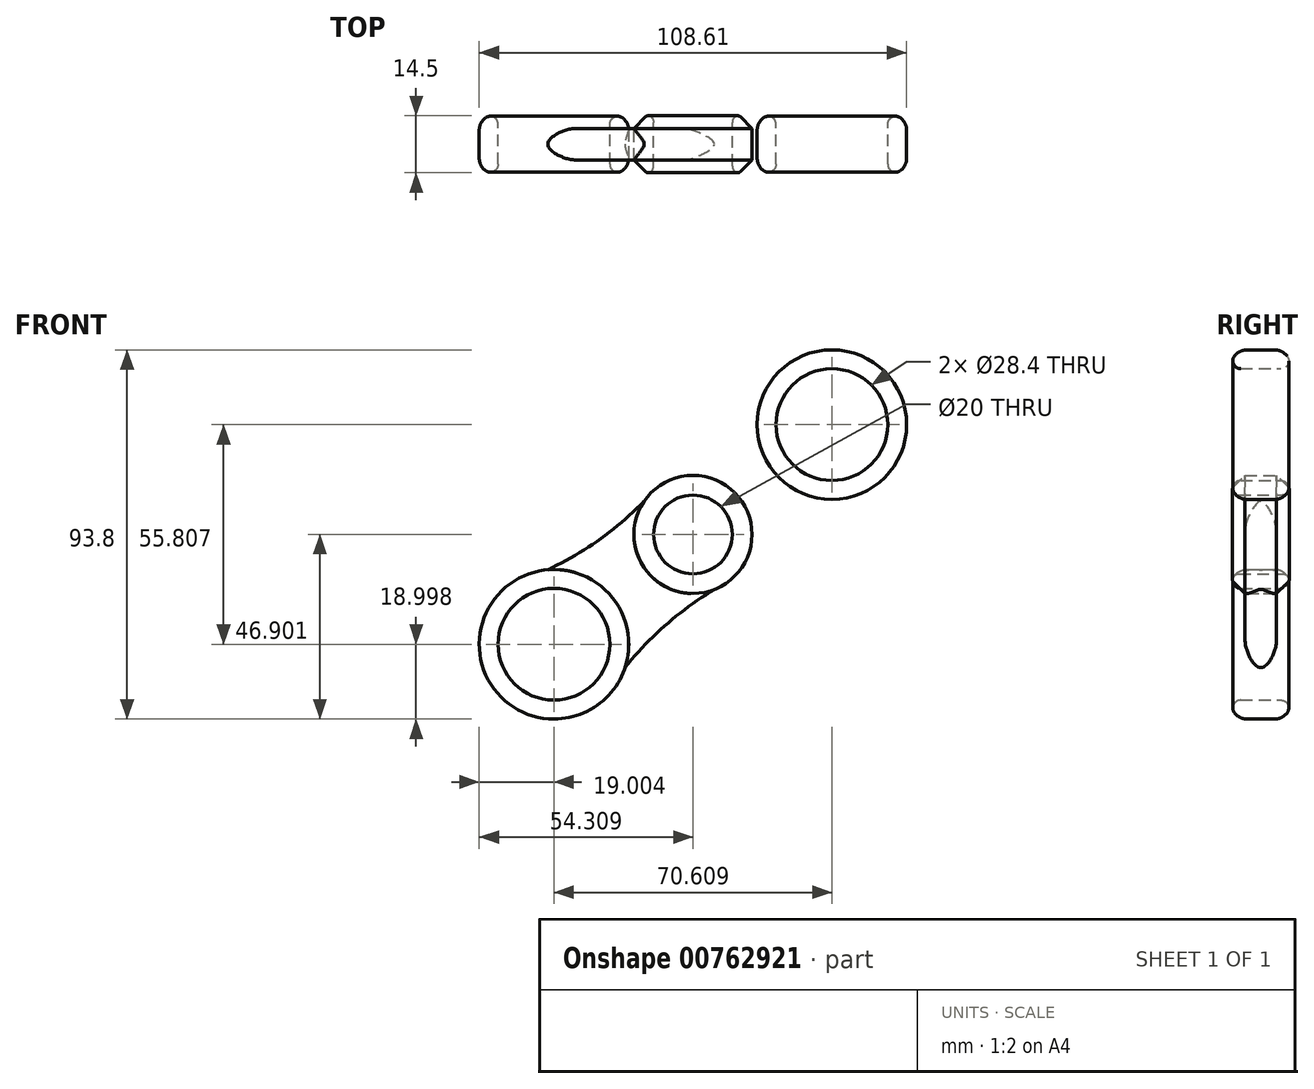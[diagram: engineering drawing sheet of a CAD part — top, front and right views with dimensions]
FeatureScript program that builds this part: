
annotation { "Feature Type Name" : "Feature", "Feature Type Description" : "" }
export const myFeature = defineFeature(function(context is Context, id is Id, definition is map)
    precondition{}
    {
        {
            var Q0;
            Q0=qCreatedBy(makeId("Front.planeOp"),FACE);
            var sketch = newSketch(context, id + "F0", { "sketchPlane" : qUnion([Q0])});
            skCircle(sketch, "E0", {"center": v(-102.67, -16) * mm, "radius": 14.2 * mm});
            skCircle(sketch, "E1", {"center": v(-32.06, 39.8) * mm, "radius": 14.2 * mm});
            skLineSegment(sketch, "E2", {"start": v(-32.06, 39.8) * mm, "end": v(-102.67, -16) * mm});
            skCircle(sketch, "E3", {"center": v(-67.36, 11.9) * mm, "radius": 15 * mm});
            skCircle(sketch, "E4", {"center": v(-102.67, -16) * mm, "radius": 19 * mm});
            skCircle(sketch, "E5", {"center": v(-32.06, 39.8) * mm, "radius": 19 * mm});
            skLineSegment(sketch, "E6", {"start": v(-79.13, 2.6) * mm, "end": v(-87.76, -4.22) * mm});
            skLineSegment(sketch, "E7", {"start": v(-87.76, -4.22) * mm, "end": v(-55.6, 21.2) * mm});
            skLineSegment(sketch, "E8", {"start": v(-55.6, 21.2) * mm, "end": v(-46.96, 28.02) * mm});
            skArc(sketch, "E9", {"start": v(-58.23, 0) * mm, "mid": v(-76.64, -13.26) * mm, "end": v(-90.88, -30.9) * mm});
            skCircle(sketch, "E10", {"center": v(-67.36, 11.9) * mm, "radius": 10 * mm});
            skArc(sketch, "E11", {"start": v(-76.66, 23.67) * mm, "mid": v(-58.15, 36.97) * mm, "end": v(-43.84, 54.71) * mm});
            skArc(sketch, "E12", {"start": v(-20.28, 24.9) * mm, "mid": v(-40.95, 15.03) * mm, "end": v(-58.23, 0) * mm});
            skArc(sketch, "E13", {"start": v(-114.45, -1.1) * mm, "mid": v(-93.88, 8.73) * mm, "end": v(-76.66, 23.67) * mm});
            skSolve(sketch);
        }
        {
            var Q0;
            {var subQ0=sQuery(id+"F0.wireOp",EDGE,"E11");var subQ1=sQuery(id+"F0.wireOp",EDGE,"E3");var subQ3=makeQuery(id+"F0.imprint","INTERSECT",VERTEX,{"derivedFrom":[subQ1,subQ0]});Q0=makeQuery(id+"F0.imprint","IMPRINT",FACE,{"disambiguationData":[TD([[makeQuery(id+"F0.imprint","IMPRINT",EDGE,{"disambiguationData":[TD([[subQ3,-1.0]])],"derivedFrom":subQ1}),1.0]])]});}
            var Q1;
            {var subQ0=sQuery(id+"F0.wireOp",EDGE,"E13");var subQ1=sQuery(id+"F0.wireOp",EDGE,"E3");var subQ3=makeQuery(id+"F0.imprint","INTERSECT",VERTEX,{"derivedFrom":[subQ1,subQ0]});Q1=makeQuery(id+"F0.imprint","IMPRINT",FACE,{"disambiguationData":[TD([[makeQuery(id+"F0.imprint","IMPRINT",EDGE,{"disambiguationData":[TD([[subQ3,1.0]])],"derivedFrom":subQ1}),1.0]])]});}
            var Q2;
            {var subQ0=sQuery(id+"F0.wireOp",EDGE,"E9");var subQ1=sQuery(id+"F0.wireOp",EDGE,"E3");var subQ3=makeQuery(id+"F0.imprint","INTERSECT",VERTEX,{"derivedFrom":[subQ1,subQ0]});Q2=makeQuery(id+"F0.imprint","IMPRINT",FACE,{"disambiguationData":[TD([[makeQuery(id+"F0.imprint","IMPRINT",EDGE,{"disambiguationData":[TD([[subQ3,-1.0]])],"derivedFrom":subQ1}),1.0]])]});}
            var Q3;
            {var subQ0=sQuery(id+"F0.wireOp",EDGE,"E12");var subQ1=sQuery(id+"F0.wireOp",EDGE,"E3");var subQ3=makeQuery(id+"F0.imprint","INTERSECT",VERTEX,{"derivedFrom":[subQ1,subQ0]});Q3=makeQuery(id+"F0.imprint","IMPRINT",FACE,{"disambiguationData":[TD([[makeQuery(id+"F0.imprint","IMPRINT",EDGE,{"disambiguationData":[TD([[subQ3,1.0]])],"derivedFrom":subQ1}),1.0]])]});}
            var Q4;
            {var subQ0=sQuery(id+"F0.wireOp",EDGE,"E13");var subQ1=sQuery(id+"F0.wireOp",EDGE,"E4");var subQ2=makeQuery(id+"F0.imprint","INTERSECT",VERTEX,{"disambiguationData":[OD(0.0)],"derivedFrom":[subQ1,subQ0]});Q4=makeQuery(id+"F0.imprint","IMPRINT",FACE,{"disambiguationData":[TD([[makeQuery(id+"F0.imprint","IMPRINT",EDGE,{"disambiguationData":[TD([[subQ2,1.0]])],"derivedFrom":subQ1}),1.0]])]});}
            var Q5;
            {var subQ0=sQuery(id+"F0.wireOp",EDGE,"E9");var subQ1=sQuery(id+"F0.wireOp",EDGE,"E4");var subQ2=makeQuery(id+"F0.imprint","INTERSECT",VERTEX,{"disambiguationData":[OD(0.0)],"derivedFrom":[subQ1,subQ0]});Q5=makeQuery(id+"F0.imprint","IMPRINT",FACE,{"disambiguationData":[TD([[makeQuery(id+"F0.imprint","IMPRINT",EDGE,{"disambiguationData":[TD([[subQ2,-1.0]])],"derivedFrom":subQ1}),1.0]])]});}
            var Q6;
            {var subQ0=sQuery(id+"F0.wireOp",EDGE,"E11");var subQ1=sQuery(id+"F0.wireOp",EDGE,"E5");var subQ2=makeQuery(id+"F0.imprint","INTERSECT",VERTEX,{"disambiguationData":[OD(0.0)],"derivedFrom":[subQ1,subQ0]});Q6=makeQuery(id+"F0.imprint","IMPRINT",FACE,{"disambiguationData":[TD([[makeQuery(id+"F0.imprint","IMPRINT",EDGE,{"disambiguationData":[TD([[subQ2,-1.0]])],"derivedFrom":subQ1}),1.0]])]});}
            var Q7;
            {var subQ0=sQuery(id+"F0.wireOp",EDGE,"E12");var subQ1=sQuery(id+"F0.wireOp",EDGE,"E5");var subQ2=makeQuery(id+"F0.imprint","INTERSECT",VERTEX,{"disambiguationData":[OD(0.0)],"derivedFrom":[subQ1,subQ0]});Q7=makeQuery(id+"F0.imprint","IMPRINT",FACE,{"disambiguationData":[TD([[makeQuery(id+"F0.imprint","IMPRINT",EDGE,{"disambiguationData":[TD([[subQ2,1.0]])],"derivedFrom":subQ1}),1.0]])]});}
            var Q8;
            Q8=makeQuery(id+"F0.imprint","IMPRINT",FACE,{"disambiguationData":[TD([[makeQuery(id+"F0.imprint","IMPRINT",EDGE,{"derivedFrom":sQuery(id+"F0.wireOp",EDGE,"E0")}),-1.0]])]});
            var Q9;
            Q9=makeQuery(id+"F0.imprint","IMPRINT",FACE,{"disambiguationData":[TD([[makeQuery(id+"F0.imprint","IMPRINT",EDGE,{"derivedFrom":sQuery(id+"F0.wireOp",EDGE,"E1")}),-1.0]])]});
            var Q10;
            {var subQ1=sQuery(id+"F0.wireOp",EDGE,"E3");var subQ7=sQuery(id+"F0.wireOp",EDGE,"E13");var subQ8=makeQuery(id+"F0.imprint","INTERSECT",VERTEX,{"derivedFrom":[subQ1,subQ7]});Q10=makeQuery(id+"F0.imprint","IMPRINT",FACE,{"disambiguationData":[TD([[makeQuery(id+"F0.imprint","IMPRINT",EDGE,{"disambiguationData":[TD([[subQ8,-1.0]])],"derivedFrom":subQ1}),1.0]])]});}
            var Q11;
            {var subQ1=sQuery(id+"F0.wireOp",EDGE,"E3");var subQ9=sQuery(id+"F0.wireOp",EDGE,"E9");var subQ10=makeQuery(id+"F0.imprint","INTERSECT",VERTEX,{"derivedFrom":[subQ1,subQ9]});Q11=makeQuery(id+"F0.imprint","IMPRINT",FACE,{"disambiguationData":[TD([[makeQuery(id+"F0.imprint","IMPRINT",EDGE,{"disambiguationData":[TD([[subQ10,1.0]])],"derivedFrom":subQ1}),1.0]])]});}
            extrude(context, id + "F1", {"entities" : qUnion([Q0, Q1, Q2, Q3, Q4, Q5, Q6, Q7, Q8, Q9, Q10, Q11]), "endBound" : BoundingType.SYMMETRIC, "depth" : 15 * mm, "offsetDistance" : 25 * mm});
        }
        {
            var Q0;
            {var subQ0=sQuery(id+"F0.wireOp",EDGE,"E8");Q0=makeQuery(id+"F0.imprint","IMPRINT",FACE,{"disambiguationData":[TD([[makeQuery(id+"F0.imprint","IMPRINT",EDGE,{"derivedFrom":subQ0}),-1.0]])]});}
            var Q1;
            {var subQ0=sQuery(id+"F0.wireOp",EDGE,"E8");Q1=makeQuery(id+"F0.imprint","IMPRINT",FACE,{"disambiguationData":[TD([[makeQuery(id+"F0.imprint","IMPRINT",EDGE,{"derivedFrom":subQ0}),1.0]])]});}
            var Q2;
            {var subQ0=sQuery(id+"F0.wireOp",EDGE,"E13");var subQ1=sQuery(id+"F0.wireOp",EDGE,"E3");var subQ2=makeQuery(id+"F0.imprint","INTERSECT",VERTEX,{"derivedFrom":[subQ1,subQ0]});Q2=makeQuery(id+"F0.imprint","IMPRINT",FACE,{"disambiguationData":[TD([[makeQuery(id+"F0.imprint","IMPRINT",EDGE,{"disambiguationData":[TD([[subQ2,-1.0]])],"derivedFrom":subQ1}),-1.0]])]});}
            var Q3;
            {var subQ0=sQuery(id+"F0.wireOp",EDGE,"E9");var subQ1=sQuery(id+"F0.wireOp",EDGE,"E3");var subQ2=makeQuery(id+"F0.imprint","INTERSECT",VERTEX,{"derivedFrom":[subQ1,subQ0]});Q3=makeQuery(id+"F0.imprint","IMPRINT",FACE,{"disambiguationData":[TD([[makeQuery(id+"F0.imprint","IMPRINT",EDGE,{"disambiguationData":[TD([[subQ2,1.0]])],"derivedFrom":subQ1}),-1.0]])]});}
            extrude(context, id + "F2", {"entities" : qUnion([Q0, Q1, Q2, Q3]), "endBound" : BoundingType.SYMMETRIC, "depth" : 8 * mm, "offsetDistance" : 25 * mm});
        }
        {
            var Q0;
            Q0=makeQuery(id+"F2.opExtrude","CAP_EDGE",EDGE,{"disambiguationData":[OSD([sQuery(id+"F0.wireOp",EDGE,"E11")])],"isStart":false});
            var Q1;
            Q1=makeQuery(id+"F2.opExtrude","CAP_EDGE",EDGE,{"disambiguationData":[OSD([sQuery(id+"F0.wireOp",EDGE,"E11")])],"isStart":true});
            var Q2;
            Q2=makeQuery(id+"F2.opExtrude","CAP_EDGE",EDGE,{"disambiguationData":[OSD([sQuery(id+"F0.wireOp",EDGE,"E13")])],"isStart":false});
            var Q3;
            Q3=makeQuery(id+"F2.opExtrude","CAP_EDGE",EDGE,{"disambiguationData":[OSD([sQuery(id+"F0.wireOp",EDGE,"E13")])],"isStart":true});
            var Q4;
            Q4=makeQuery(id+"F2.opExtrude","CAP_EDGE",EDGE,{"disambiguationData":[OSD([sQuery(id+"F0.wireOp",EDGE,"E9")])],"isStart":false});
            var Q5;
            Q5=makeQuery(id+"F2.opExtrude","CAP_EDGE",EDGE,{"disambiguationData":[OSD([sQuery(id+"F0.wireOp",EDGE,"E9")])],"isStart":true});
            var Q6;
            Q6=makeQuery(id+"F2.opExtrude","CAP_EDGE",EDGE,{"disambiguationData":[OSD([sQuery(id+"F0.wireOp",EDGE,"E12")])],"isStart":true});
            var Q7;
            Q7=makeQuery(id+"F2.opExtrude","CAP_EDGE",EDGE,{"disambiguationData":[OSD([sQuery(id+"F0.wireOp",EDGE,"E12")])],"isStart":false});
            fillet(context, id + "F3", {"entities" : qUnion([Q0, Q1, Q2, Q3, Q4, Q5, Q6, Q7]), "radius" : 4 * mm, "tangentPropagation" : true, "allowEdgeOverflow" : false});
        }
        {
            var Q0;
            Q0=makeQuery(id+"F1.opExtrude","CAP_EDGE",EDGE,{"disambiguationData":[OSD([sQuery(id+"F0.wireOp",EDGE,"E10")])],"isStart":false});
            var Q1;
            Q1=makeQuery(id+"F1.opExtrude","CAP_EDGE",EDGE,{"disambiguationData":[OSD([sQuery(id+"F0.wireOp",EDGE,"E10")])],"isStart":true});
            fillet(context, id + "F4", {"entities" : qUnion([Q0, Q1]), "radius" : 2 * mm, "tangentPropagation" : true, "allowEdgeOverflow" : false});
        }
        {
            var Q0;
            Q0=makeQuery(id+"F1.opExtrude","CAP_EDGE",EDGE,{"disambiguationData":[OSD([sQuery(id+"F0.wireOp",EDGE,"E5")])],"isStart":false});
            var Q1;
            Q1=makeQuery(id+"F1.opExtrude","CAP_EDGE",EDGE,{"disambiguationData":[OSD([sQuery(id+"F0.wireOp",EDGE,"E5")])],"isStart":true});
            var Q2;
            Q2=makeQuery(id+"F1.opExtrude","CAP_EDGE",EDGE,{"disambiguationData":[OSD([sQuery(id+"F0.wireOp",EDGE,"E4")])],"isStart":false});
            var Q3;
            Q3=makeQuery(id+"F1.opExtrude","CAP_EDGE",EDGE,{"disambiguationData":[OSD([sQuery(id+"F0.wireOp",EDGE,"E4")])],"isStart":true});
            fillet(context, id + "F5", {"entities" : qUnion([Q0, Q1, Q2, Q3]), "radius" : 4 * mm, "tangentPropagation" : true, "allowEdgeOverflow" : false});
        }
        {
            var Q0;
            Q0=makeQuery(id+"F1.opExtrude","CAP_EDGE",EDGE,{"disambiguationData":[OSD([sQuery(id+"F0.wireOp",EDGE,"E0")])],"isStart":true});
            var Q1;
            Q1=makeQuery(id+"F1.opExtrude","CAP_EDGE",EDGE,{"disambiguationData":[OSD([sQuery(id+"F0.wireOp",EDGE,"E1")])],"isStart":true});
            var Q2;
            Q2=makeQuery(id+"F1.opExtrude","CAP_EDGE",EDGE,{"disambiguationData":[OSD([sQuery(id+"F0.wireOp",EDGE,"E1")])],"isStart":false});
            var Q3;
            Q3=makeQuery(id+"F1.opExtrude","CAP_EDGE",EDGE,{"disambiguationData":[OSD([sQuery(id+"F0.wireOp",EDGE,"E0")])],"isStart":false});
            fillet(context, id + "F6", {"entities" : qUnion([Q0, Q1, Q2, Q3]), "radius" : 2 * mm, "tangentPropagation" : true, "allowEdgeOverflow" : false});
        }
        {
            var Q0;
            Q0=makeQuery(id+"F1.opExtrude","CAP_EDGE",EDGE,{"disambiguationData":[OSD([sQuery(id+"F0.wireOp",EDGE,"E3")])],"isStart":true});
            var Q1;
            Q1=makeQuery(id+"F1.opExtrude","CAP_EDGE",EDGE,{"disambiguationData":[OSD([sQuery(id+"F0.wireOp",EDGE,"E3")])],"isStart":false});
            chamfer(context, id + "F7", {"entities" : qUnion([Q0, Q1]), "width" : 3.5 * mm, "tangentPropagation" : true});
        }
        {
            var Q0;
            {var subQ0=sQuery(id+"F0.wireOp",EDGE,"E10");Q0=makeQuery(id+"F7.opChamfer","BLEND_EDGE",EDGE,{"blendedFrom":[makeQuery(id+"F1.opExtrude","CAP_EDGE",EDGE,{"disambiguationData":[OSD([sQuery(id+"F0.wireOp",EDGE,"E3")])],"isStart":true}),makeQuery(id+"F4.opFillet","BLEND_FACE",FACE,{"disambiguationData":[OSD([subQ0]),TDD([makeQuery(id+"F1.opExtrude","CAP_EDGE",EDGE,{"disambiguationData":[OSD([subQ0])],"isStart":true})])]})],"blendedInto":[makeQuery(id+"F4.opFillet","BLEND_FACE",FACE,{"disambiguationData":[OSD([subQ0]),TDD([makeQuery(id+"F1.opExtrude","CAP_EDGE",EDGE,{"disambiguationData":[OSD([subQ0])],"isStart":true})])]})]});}
            var Q1;
            {var subQ0=sQuery(id+"F0.wireOp",EDGE,"E10");Q1=makeQuery(id+"F7.opChamfer","BLEND_EDGE",EDGE,{"blendedFrom":[makeQuery(id+"F1.opExtrude","CAP_EDGE",EDGE,{"disambiguationData":[OSD([sQuery(id+"F0.wireOp",EDGE,"E3")])],"isStart":false}),makeQuery(id+"F4.opFillet","BLEND_FACE",FACE,{"disambiguationData":[OSD([subQ0]),TDD([makeQuery(id+"F1.opExtrude","CAP_EDGE",EDGE,{"disambiguationData":[OSD([subQ0])],"isStart":false})])]})],"blendedInto":[makeQuery(id+"F4.opFillet","BLEND_FACE",FACE,{"disambiguationData":[OSD([subQ0]),TDD([makeQuery(id+"F1.opExtrude","CAP_EDGE",EDGE,{"disambiguationData":[OSD([subQ0])],"isStart":false})])]})]});}
            fillet(context, id + "F8", {"entities" : qUnion([Q0, Q1]), "radius" : 1 * mm, "tangentPropagation" : true, "allowEdgeOverflow" : false});
        }
    });
